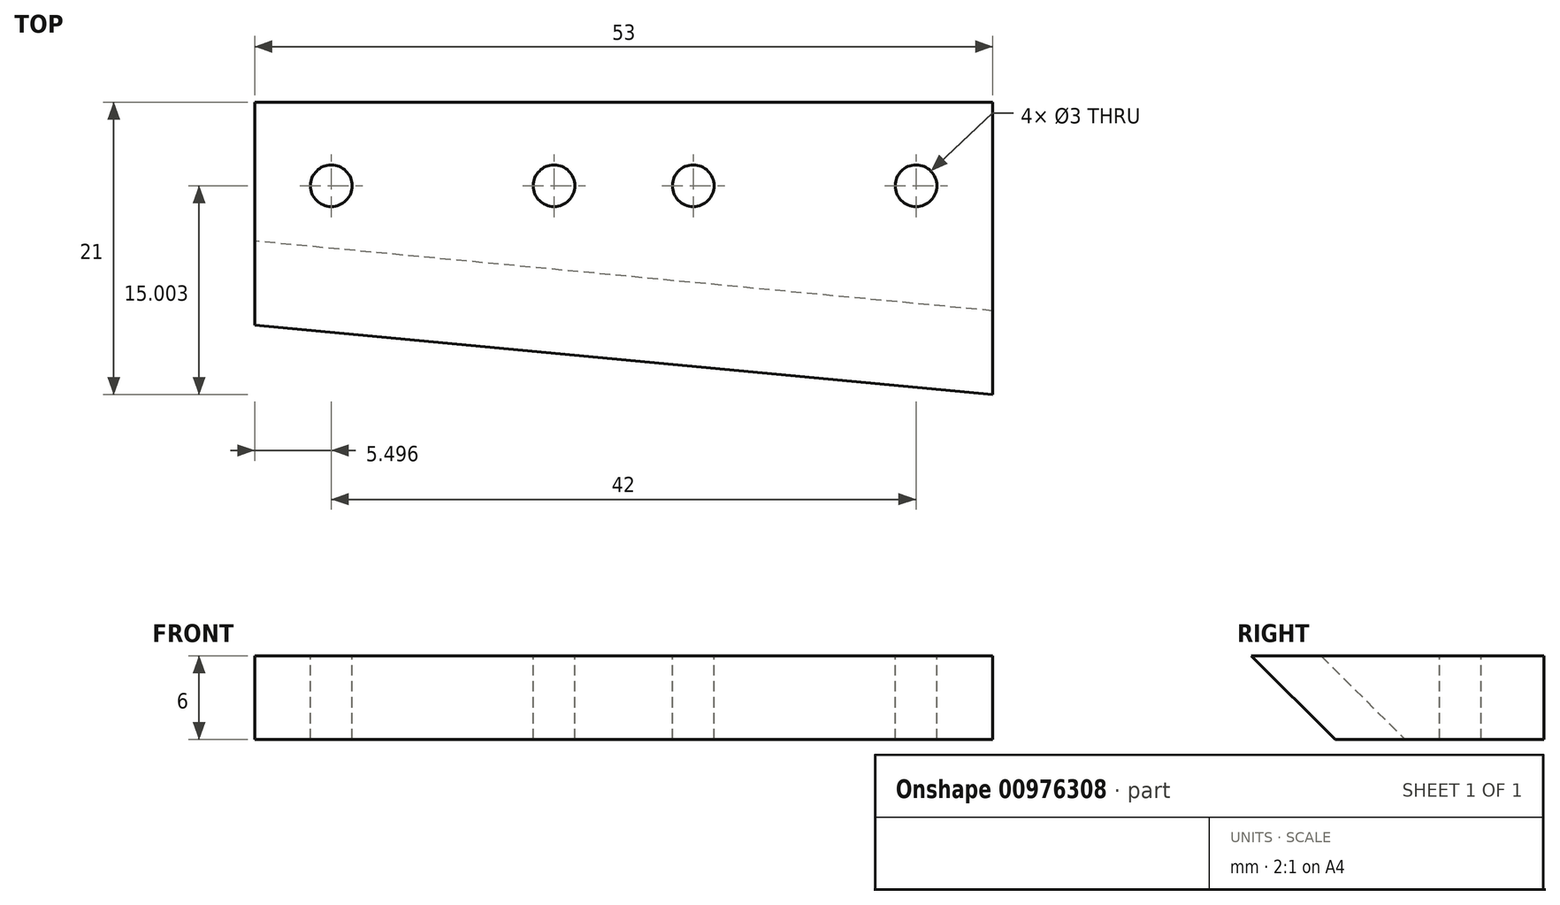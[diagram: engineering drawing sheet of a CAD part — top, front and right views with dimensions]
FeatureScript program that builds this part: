
annotation { "Feature Type Name" : "Feature", "Feature Type Description" : "" }
export const myFeature = defineFeature(function(context is Context, id is Id, definition is map)
    precondition{}
    {
        {
            var Q0;
            Q0=qCreatedBy(makeId("Top.planeOp"),FACE);
            var sketch = newSketch(context, id + "F0", { "sketchPlane" : qUnion([Q0])});
            skLineSegment(sketch, "E0.bottom", {"start": v(-3.73, 5.91) * mm, "end": v(49.27, 5.91) * mm});
            skLineSegment(sketch, "E0.top", {"start": v(-3.73, -15.09) * mm, "end": v(49.27, -15.09) * mm});
            skLineSegment(sketch, "E0.left", {"start": v(-3.73, 5.91) * mm, "end": v(-3.73, -15.09) * mm});
            skLineSegment(sketch, "E0.right", {"start": v(49.27, 5.91) * mm, "end": v(49.27, -15.09) * mm});
            skLineSegment(sketch, "E1", {"start": v(-3.73, -10.09) * mm, "end": v(49.27, -15.09) * mm});
            skSolve(sketch);
        }
        {
            var Q0;
            {var subQ0=sQuery(id+"F0.wireOp",EDGE,"E0.bottom");Q0=makeQuery(id+"F0.imprint","IMPRINT",FACE,{"disambiguationData":[TD([[makeQuery(id+"F0.imprint","IMPRINT",EDGE,{"derivedFrom":subQ0}),-1.0]])]});}
            extrude(context, id + "F1", {"entities" : qUnion([Q0]), "depth" : 6 * mm, "offsetDistance" : 25 * mm});
        }
        {
            var Q0;
            Q0=makeQuery(id+"F1.opExtrude","CAP_EDGE",EDGE,{"disambiguationData":[OSD([sQuery(id+"F0.wireOp",EDGE,"E1")])],"isStart":true});
            chamfer(context, id + "F2", {"entities" : qUnion([Q0]), "width" : 6 * mm, "tangentPropagation" : true});
        }
        {
            var Q0;
            Q0=makeQuery(id+"F1.opExtrude","CAP_FACE",FACE,{"disambiguationData":[OSD([sQuery(id+"F0.wireOp",EDGE,"E0.bottom"),sQuery(id+"F0.wireOp",EDGE,"E0.left"),sQuery(id+"F0.wireOp",EDGE,"E0.right"),sQuery(id+"F0.wireOp",EDGE,"E1")])],"isStart":false});
            var sketch = newSketch(context, id + "F3", { "sketchPlane" : qUnion([Q0])});
            skCircle(sketch, "E2", {"center": v(1.77, -0.09) * mm, "radius": 1.5 * mm});
            skCircle(sketch, "E3", {"center": v(17.77, -0.09) * mm, "radius": 1.5 * mm});
            skCircle(sketch, "E4", {"center": v(27.77, -0.09) * mm, "radius": 1.5 * mm});
            skCircle(sketch, "E5", {"center": v(43.77, -0.09) * mm, "radius": 1.5 * mm});
            skSolve(sketch);
        }
        {
            var Q0;
            Q0=qSketchRegion(id+"F3",true);
            extrude(context, id + "F4", {"entities" : qUnion([Q0]), "operationType" : NewBodyOperationType.REMOVE, "endBound" : BoundingType.UP_TO_NEXT, "oppositeDirection" : true, "depth" : 25 * mm, "offsetDistance" : 25 * mm});
        }
    });
